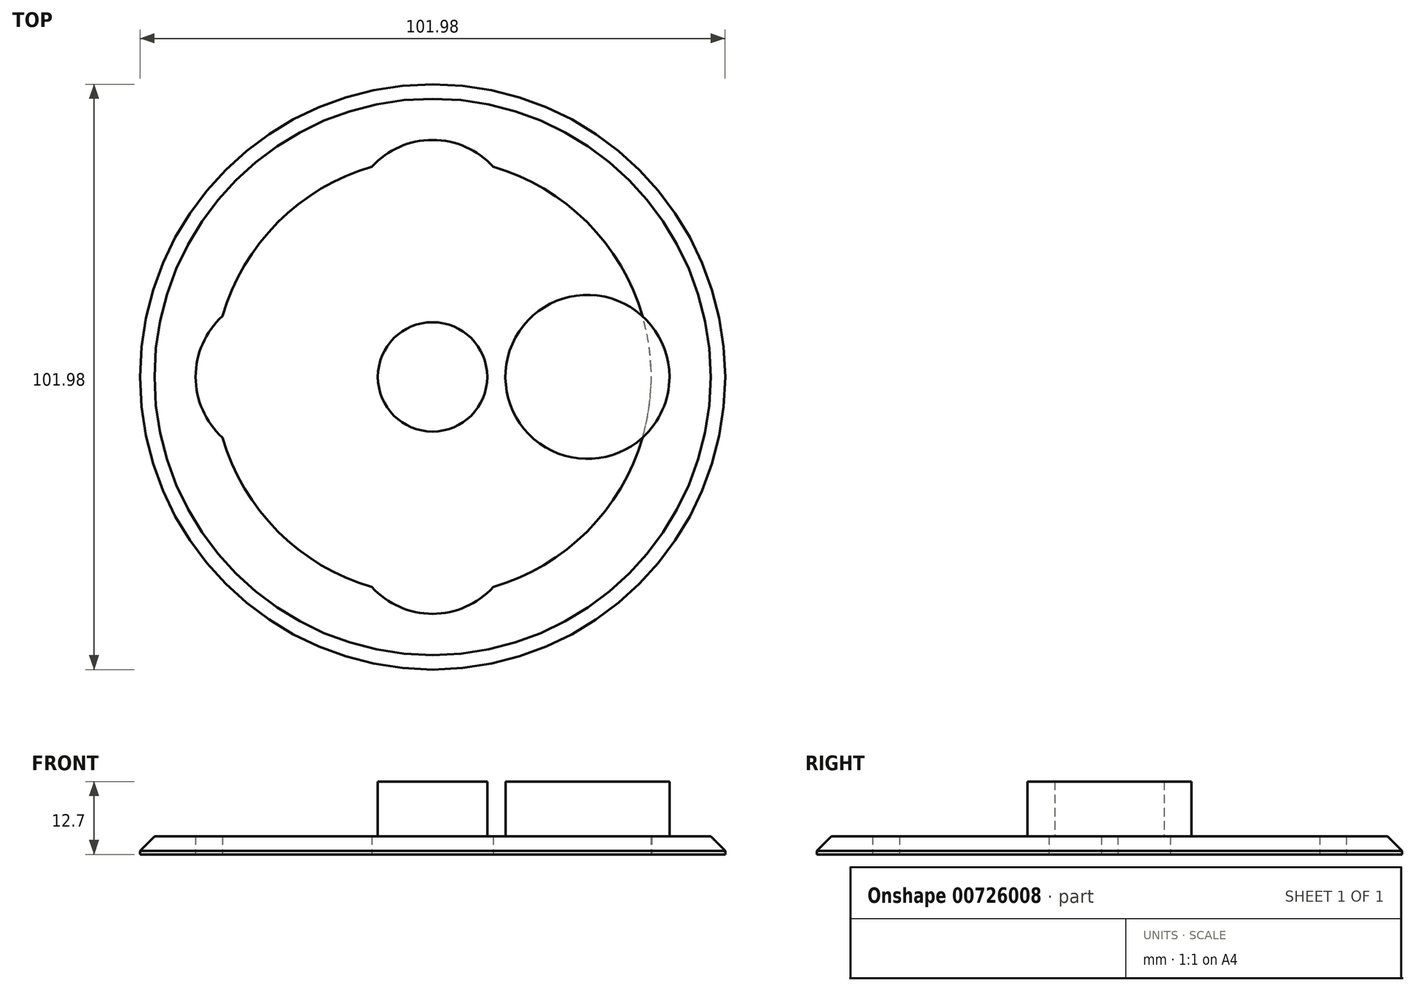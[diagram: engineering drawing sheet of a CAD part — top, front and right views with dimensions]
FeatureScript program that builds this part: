
annotation { "Feature Type Name" : "Feature", "Feature Type Description" : "" }
export const myFeature = defineFeature(function(context is Context, id is Id, definition is map)
    precondition{}
    {
        {
            var Q0;
            Q0=qCreatedBy(makeId("Top.planeOp"),FACE);
            var sketch = newSketch(context, id + "F0", { "sketchPlane" : qUnion([Q0])});
            skCircle(sketch, "E0", {"center": v(0, 0) * mm, "radius": 51 * mm});
            skCircle(sketch, "E1", {"center": v(0, 0) * mm, "radius": 38.1 * mm});
            skCircle(sketch, "E2", {"center": v(0, 0) * mm, "radius": 6.41 * mm});
            skCircle(sketch, "E3", {"center": v(0, 0) * mm, "radius": 26.99 * mm, "construction": true});
            skCircle(sketch, "E4", {"center": v(26.99, 0) * mm, "radius": 11.18 * mm});
            skCircle(sketch, "E5", {"center": v(0, 26.99) * mm, "radius": 14.29 * mm});
            skCircle(sketch, "E6", {"center": v(-26.99, 0) * mm, "radius": 14.29 * mm});
            skCircle(sketch, "E7", {"center": v(0, -26.99) * mm, "radius": 14.29 * mm});
            skSolve(sketch);
        }
        {
            var Q0;
            Q0=makeQuery(id+"F0.imprint","IMPRINT",FACE,{"disambiguationData":[TD([[makeQuery(id+"F0.imprint","IMPRINT",EDGE,{"derivedFrom":sQuery(id+"F0.wireOp",EDGE,"E0")}),1.0]])]});
            var Q1;
            Q1=makeQuery(id+"F0.imprint","IMPRINT",FACE,{"disambiguationData":[TD([[makeQuery(id+"F0.imprint","IMPRINT",EDGE,{"derivedFrom":sQuery(id+"F0.wireOp",EDGE,"ebed6062-50ca-43e5-a92f-e91f17315492.3.0")}),1.0]])]});
            var Q2;
            Q2=makeQuery(id+"F0.imprint","IMPRINT",FACE,{"disambiguationData":[TD([[makeQuery(id+"F0.imprint","IMPRINT",EDGE,{"derivedFrom":sQuery(id+"F0.wireOp",EDGE,"c8b00ff3-3790-418a-a299-005cbc117579")}),1.0]])]});
            var Q3;
            Q3=makeQuery(id+"F0.imprint","IMPRINT",FACE,{"disambiguationData":[TD([[makeQuery(id+"F0.imprint","IMPRINT",EDGE,{"derivedFrom":sQuery(id+"F0.wireOp",EDGE,"ebed6062-50ca-43e5-a92f-e91f17315492.1.0")}),1.0]])]});
            var Q4;
            Q4=makeQuery(id+"F0.imprint","IMPRINT",FACE,{"disambiguationData":[TD([[makeQuery(id+"F0.imprint","IMPRINT",EDGE,{"derivedFrom":sQuery(id+"F0.wireOp",EDGE,"ebed6062-50ca-43e5-a92f-e91f17315492.2.0")}),1.0]])]});
            var Q5;
            Q5=makeQuery(id+"F0.imprint","IMPRINT",FACE,{"disambiguationData":[TD([[makeQuery(id+"F0.imprint","IMPRINT",EDGE,{"derivedFrom":sQuery(id+"F0.wireOp",EDGE,"E2")}),-1.0]])]});
            extrude(context, id + "F1", {"entities" : qUnion([Q0, Q1, Q2, Q3, Q4, Q5]), "depth" : 3.17 * mm, "offsetDistance" : 25.4 * mm});
        }
        {
            var Q0;
            Q0=makeQuery(id+"F1.opExtrude","CAP_FACE",FACE,{"disambiguationData":[OSD([sQuery(id+"F0.wireOp",EDGE,"E0"),sQuery(id+"F0.wireOp",EDGE,"E2"),sQuery(id+"F0.wireOp",EDGE,"E4")])],"isStart":false});
            var sketch = newSketch(context, id + "F2", { "sketchPlane" : qUnion([Q0])});
            skCircle(sketch, "E8", {"center": v(0, 0) * mm, "radius": 9.53 * mm});
            skCircle(sketch, "E9", {"center": v(26.99, 0) * mm, "radius": 14.29 * mm});
            skSolve(sketch);
        }
        {
            var Q0;
            Q0=makeQuery(id+"F2.imprint","IMPRINT",FACE,{"disambiguationData":[TD([[makeQuery(id+"F2.imprint","IMPRINT",EDGE,{"derivedFrom":sQuery(id+"F2.wireOp",EDGE,"E8")}),1.0]])]});
            var Q1;
            Q1=makeQuery(id+"F2.imprint","IMPRINT",FACE,{"disambiguationData":[TD([[makeQuery(id+"F2.imprint","IMPRINT",EDGE,{"derivedFrom":sQuery(id+"F2.wireOp",EDGE,"E9")}),1.0]])]});
            extrude(context, id + "F3", {"entities" : qUnion([Q0, Q1]), "operationType" : NewBodyOperationType.ADD, "depth" : 9.52 * mm, "offsetDistance" : 25.4 * mm});
        }
        {
            var Q0;
            Q0=makeQuery(id+"F1.opExtrude","CAP_EDGE",EDGE,{"disambiguationData":[OSD([sQuery(id+"F0.wireOp",EDGE,"E0")])],"isStart":false});
            chamfer(context, id + "F4", {"entities" : qUnion([Q0]), "width" : 2.54 * mm, "tangentPropagation" : true});
        }
    });
